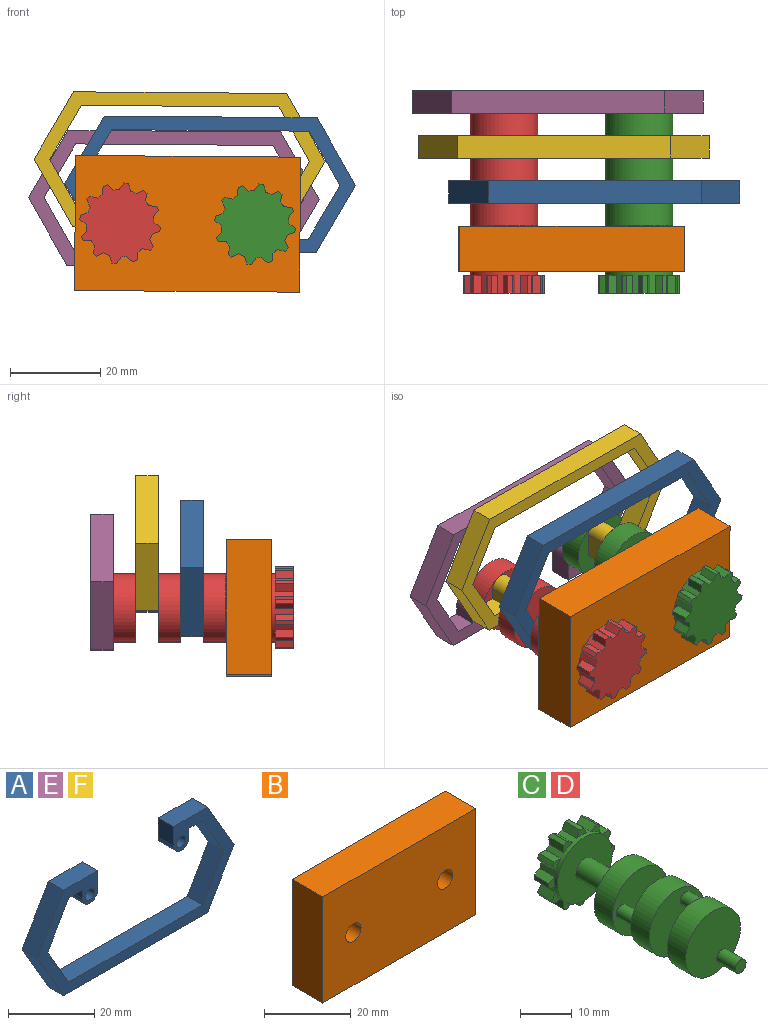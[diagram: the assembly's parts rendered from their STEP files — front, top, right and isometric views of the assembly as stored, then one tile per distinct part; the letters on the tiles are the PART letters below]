
ASSEMBLY  parts=6 mates=8
PART A: 24 faces, bbox 64.6x5x30 mm
  f0: plane 11.16x5mm, normal (0,0,1), area 55.8mm2, adj f1,f2,f11,f17
  f1: plane 64.64x30mm, normal (0,-1,0), area 415.1mm2, adj f0,f3,f4,f5,f6,f7,f8,f9
  f2: plane 64.64x30mm, normal (0,1,0), area 415.1mm2, adj f0,f3,f4,f5,f6,f7,f8,f9
  f3: plane 5x4.43mm, normal (0,0,-1), area 22.1mm2, adj f1,f2,f6,f22
  f4: plane 12x6.93mm, normal (0.87,0,-0.5), area 69.3mm2, adj f1,f2,f5,f15
  f5: plane 5x4.43mm, normal (0,0,-1), area 22.1mm2, adj f1,f2,f4,f19
  f6: plane 12x6.93mm, normal (-0.87,0,-0.5), area 69.3mm2, adj f1,f2,f3,f7
  f7: plane 12x6.93mm, normal (-0.87,0,0.5), area 69.3mm2, adj f1,f2,f6,f8
  f8: plane 43.86x5mm, normal (0,0,1), area 219.3mm2, adj f1,f2,f7,f15
  f9: plane 15x8.66mm, normal (0.87,0,0.5), area 86.6mm2, adj f1,f2,f10,f14
  f10: plane 11.16x5mm, normal (0,0,1), area 55.8mm2, adj f1,f2,f9,f20
  f11: plane 15x8.66mm, normal (-0.87,0,0.5), area 86.6mm2, adj f0,f1,f2,f12
  f12: plane 15x8.66mm, normal (-0.87,0,-0.5), area 86.6mm2, adj f1,f2,f11,f13
  f13: plane 47.32x5mm, normal (0,0,-1), area 236.6mm2, adj f1,f2,f12,f14
  f14: plane 15x8.66mm, normal (0.87,0,-0.5), area 86.6mm2, adj f1,f2,f9,f13
  f15: plane 12x6.93mm, normal (0.87,0,0.5), area 69.3mm2, adj f1,f2,f4,f8
  f16: cylinder r=2.5mm len=5mm, axis (0,-1,0), area 39.3mm2, adj f1,f2,f17,f19
  f17: plane 5.5x5mm, normal (1,0,0), area 27.5mm2, adj f0,f1,f2,f16
  f18: cylinder r=1.55mm len=5mm, axis (0,-1,0), area 48.7mm2, adj f1,f2
  f19: plane 5x2.5mm, normal (-1,0,0), area 12.5mm2, adj f1,f2,f5,f16
  f20: plane 5.5x5mm, normal (-1,0,0), area 27.5mm2, adj f1,f2,f10,f21
  f21: cylinder r=2.5mm len=5mm, axis (0,-1,0), area 39.3mm2, adj f1,f2,f20,f22
  f22: plane 5x2.5mm, normal (1,0,0), area 12.5mm2, adj f1,f2,f3,f21
  f23: cylinder r=1.55mm len=5mm, axis (0,-1,0), area 48.7mm2, adj f1,f2
PART B: 8 faces, bbox 50x10x30 mm
  f0: plane 50x10mm, normal (0,0,-1), area 500mm2, adj f1,f5,f6,f7
  f1: plane 30x10mm, normal (1,0,0), area 300mm2, adj f0,f2,f6,f7
  f2: plane 50x10mm, normal (0,0,1), area 500mm2, adj f1,f5,f6,f7
  f3: cylinder r=2.5mm len=10mm, axis (0,1,0), area 157.1mm2, adj f6,f7
  f4: cylinder r=2.5mm len=10mm, axis (0,1,0), area 157.1mm2, adj f6,f7
  f5: plane 30x10mm, normal (-1,0,0), area 300mm2, adj f0,f2,f6,f7
  f6: plane 50x30mm, normal (0,-1,0), area 1460.7mm2, adj f0,f1,f2,f3,f4,f5
  f7: plane 50x30mm, normal (0,1,0), area 1460.7mm2, adj f0,f1,f2,f3,f4,f5
PART C: 65 faces, bbox 18x45x18 mm
  f0: cylinder r=2.45mm len=10.1mm, axis (0,1,0), area 155.5mm2, adj f3,f14
  f1: cylinder r=7.5mm len=15mm, axis (0,1,0), area 235.6mm2, adj f2,f3
  f2: plane 15x15mm, normal (0,-1,0), area 169.6mm2, adj f1,f4
  f3: plane 15x15mm, normal (0,1,0), area 157.9mm2, adj f0,f1
  f4: cylinder r=1.5mm len=5mm, axis (0,1,0), area 47.1mm2, adj f2,f7
  f5: cylinder r=7.5mm len=15mm, axis (0,1,0), area 235.6mm2, adj f6,f7
  f6: plane 15x15mm, normal (0,-1,0), area 169.6mm2, adj f5,f8
  f7: plane 15x15mm, normal (0,1,0), area 169.6mm2, adj f4,f5
  f8: cylinder r=1.5mm len=5mm, axis (0,1,0), area 47.1mm2, adj f6,f11
  f9: cylinder r=7.5mm len=15mm, axis (0,1,0), area 235.6mm2, adj f10,f11
  f10: plane 15x15mm, normal (0,-1,0), area 169.6mm2, adj f9,f12
  f11: plane 15x15mm, normal (0,1,0), area 169.6mm2, adj f8,f9
  f12: cylinder r=1.5mm len=5mm, axis (0,1,0), area 47.1mm2, adj f10,f13
  f13: plane 3x3mm, normal (0,-1,0), area 7.1mm2, adj f12
  f14: plane 15x15mm, normal (0,-1,0), area 157.9mm2, adj f0,f64
  f15: plane 4x0.87mm, normal (-0.87,0,-0.5), area 4mm2, adj f57,f58,f59,f60
  f16: plane 4x0.87mm, normal (-0.5,0,-0.87), area 4mm2, adj f54,f55,f56,f60
  f17: plane 4x1mm, normal (0,0,-1), area 4mm2, adj f51,f52,f53,f60
  f18: plane 4x0.87mm, normal (0.5,0,-0.87), area 4mm2, adj f48,f49,f50,f60
  f19: plane 4x0.87mm, normal (0.87,0,-0.5), area 4mm2, adj f45,f46,f47,f60
  f20: plane 4x1mm, normal (1,0,0), area 4mm2, adj f42,f43,f44,f60
  f21: plane 4x0.87mm, normal (0.87,0,0.5), area 4mm2, adj f39,f40,f41,f60
  f22: plane 4x0.87mm, normal (0.5,0,0.87), area 4mm2, adj f36,f37,f38,f60
  f23: plane 4x1mm, normal (0,0,1), area 4mm2, adj f33,f34,f35,f60
  f24: plane 4x0.87mm, normal (-0.5,0,0.87), area 4mm2, adj f30,f31,f32,f60
  f25: plane 4x0.87mm, normal (-0.87,0,0.5), area 4mm2, adj f27,f28,f29,f60
  f26: plane 4x1mm, normal (-1,0,0), area 4mm2, adj f60,f61,f62,f63
  f27: plane 4x1.5mm, normal (-0.83,0,-0.55), area 7.2mm2, adj f25,f28,f60,f64
  f28: plane 2.36x2.3mm, normal (0,-1,0), area 2.7mm2, adj f25,f27,f29,f64
  f29: plane 4x1.8mm, normal (0.06,0,1), area 7.2mm2, adj f25,f28,f60,f64
  f30: plane 4x1.8mm, normal (-1,0,-0.06), area 7.2mm2, adj f24,f31,f60,f64
  f31: plane 2.36x2.3mm, normal (0,-1,0), area 2.7mm2, adj f24,f30,f32,f64
  f32: plane 4x1.5mm, normal (0.55,0,0.83), area 7.2mm2, adj f24,f31,f60,f64
  f33: plane 4x1.61mm, normal (-0.9,0,0.44), area 7.2mm2, adj f23,f34,f60,f64
  f34: plane 2.6x1.61mm, normal (0,-1,0), area 2.7mm2, adj f23,f33,f35,f64
  f35: plane 4x1.61mm, normal (0.9,0,0.44), area 7.2mm2, adj f23,f34,f60,f64
  f36: plane 4x1.5mm, normal (-0.55,0,0.83), area 7.2mm2, adj f22,f37,f60,f64
  f37: plane 2.36x2.3mm, normal (0,-1,0), area 2.7mm2, adj f22,f36,f38,f64
  f38: plane 4x1.8mm, normal (1,0,-0.06), area 7.2mm2, adj f22,f37,f60,f64
  f39: plane 4x1.8mm, normal (-0.06,0,1), area 7.2mm2, adj f21,f40,f60,f64
  f40: plane 2.36x2.3mm, normal (0,-1,0), area 2.7mm2, adj f21,f39,f41,f64
  f41: plane 4x1.5mm, normal (0.83,0,-0.55), area 7.2mm2, adj f21,f40,f60,f64
  f42: plane 4x1.61mm, normal (0.44,0,0.9), area 7.2mm2, adj f20,f43,f60,f64
  f43: plane 2.6x1.61mm, normal (0,-1,0), area 2.7mm2, adj f20,f42,f44,f64
  f44: plane 4x1.61mm, normal (0.44,0,-0.9), area 7.2mm2, adj f20,f43,f60,f64
  f45: plane 4x1.5mm, normal (0.83,0,0.55), area 7.2mm2, adj f19,f46,f60,f64
  f46: plane 2.36x2.3mm, normal (0,-1,0), area 2.7mm2, adj f19,f45,f47,f64
  f47: plane 4x1.8mm, normal (-0.06,0,-1), area 7.2mm2, adj f19,f46,f60,f64
  f48: plane 4x1.8mm, normal (1,0,0.06), area 7.2mm2, adj f18,f49,f60,f64
  f49: plane 2.36x2.3mm, normal (0,-1,0), area 2.7mm2, adj f18,f48,f50,f64
  f50: plane 4x1.5mm, normal (-0.55,0,-0.83), area 7.2mm2, adj f18,f49,f60,f64
  f51: plane 4x1.61mm, normal (0.9,0,-0.44), area 7.2mm2, adj f17,f52,f60,f64
  f52: plane 2.6x1.61mm, normal (0,-1,0), area 2.7mm2, adj f17,f51,f53,f64
  f53: plane 4x1.61mm, normal (-0.9,0,-0.44), area 7.2mm2, adj f17,f52,f60,f64
  f54: plane 4x1.5mm, normal (0.55,0,-0.83), area 7.2mm2, adj f16,f55,f60,f64
  f55: plane 2.36x2.3mm, normal (0,-1,0), area 2.7mm2, adj f16,f54,f56,f64
  f56: plane 4x1.8mm, normal (-1,0,0.06), area 7.2mm2, adj f16,f55,f60,f64
  f57: plane 4x1.8mm, normal (0.06,0,-1), area 7.2mm2, adj f15,f58,f60,f64
  f58: plane 2.36x2.3mm, normal (0,-1,0), area 2.7mm2, adj f15,f57,f59,f64
  f59: plane 4x1.5mm, normal (-0.83,0,0.55), area 7.2mm2, adj f15,f58,f60,f64
  f60: plane 18x18mm, normal (0,1,0), area 209.2mm2, adj f15,f16,f17,f18,f19,f20,f21,f22
  f61: plane 4x1.61mm, normal (-0.44,0,-0.9), area 7.2mm2, adj f26,f60,f62,f64
  f62: plane 2.6x1.61mm, normal (0,-1,0), area 2.7mm2, adj f26,f61,f63,f64
  f63: plane 4x1.61mm, normal (-0.44,0,0.9), area 7.2mm2, adj f26,f60,f62,f64
  f64: cylinder r=7.5mm len=15mm, axis (0,-1,0), area 105.6mm2, adj f14,f27,f28,f29,f30,f31,f32,f33
PART D: same geometry as C
PART E: same geometry as A
PART F: same geometry as A
PLACE A rot(axis=(-1,0,0),180deg) t=(-83.41,-65.4,25.52)mm
PLACE B rot(axis=(0,1,0),0.4deg) t=(-88.42,-70.5,16.76)mm fixed
PLACE C rot(axis=(-0.07,0,-1),180deg) t=(-73.42,-80.4,16.65)mm
PLACE D rot(axis=(-0.07,0,-1),180deg) t=(-103.42,-80.4,16.87)mm
PLACE E rot(axis=(-1,0,0),180deg) t=(-91.46,-45.4,22.35)mm
PLACE F rot(axis=(-1,0,0),180deg) t=(-90.18,-55.4,30.91)mm
MATE revolute D.f64 <-> B.f4  axis (0,1,0) through (-103.42,-80.5,16.87)mm
MATE revolute E.f21 <-> C.f12  axis (0,1,0) through (-76.54,-40.4,12.74)mm
MATE revolute D.f4 <-> A.f16  axis (0,1,0) through (-98.48,-65.4,16.13)mm
MATE revolute E.f16 <-> D.f12  axis (0,1,0) through (-106.54,-40.4,12.96)mm
MATE revolute D.f8 <-> F.f16  axis (0,1,0) through (-105.25,-55.4,21.53)mm
MATE revolute C.f64 <-> B.f3  axis (0,1,0) through (-73.42,-80.5,16.65)mm
MATE revolute F.f21 <-> C.f8  axis (0,1,0) through (-75.25,-50.4,21.3)mm
MATE revolute C.f4 <-> A.f21  axis (0,1,0) through (-68.48,-65.4,15.9)mm
